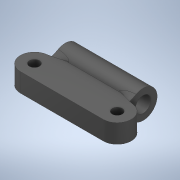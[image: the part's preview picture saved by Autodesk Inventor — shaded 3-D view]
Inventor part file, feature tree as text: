
AUTODESK INVENTOR PART (.ipt)
format: ipt  version: 2020.4 (Build 244396010, 396A)  size: 239,104 bytes
history: native  units: in
note: dims shown in document units (in); Inventor stores cm internally (conversion verified against a paired STEP export)
features: extrude x1, sketch x1
ambient origin geometry x8: Origin, YZ Plane, XZ Plane, XY Plane, X Axis, Y Axis, Z Axis, Center Point
bodies: Solid2 (feature_tree), Solid1 (feature_tree)
feature tree (2):
  extrude  "Extrusion1"  Depth=0.3937in
  sketch  "Sketch1"  dims[d0=0.126in d1=0.126in d2=0.3937in d3=0.0in d4=0.0197in d5=1.9685in]
